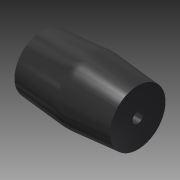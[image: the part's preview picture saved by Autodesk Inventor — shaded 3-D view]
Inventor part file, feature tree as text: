
AUTODESK INVENTOR PART (.ipt)
format: ipt  version: 2014 SP2 (Build 180246200, 246)  size: 101,376 bytes
history: native  units: mm
features: sketch x5, extrude x2, chamfer x2, fillet x1, projected_geometry x1
ambient origin geometry x8: Origin, YZ Plane, XZ Plane, XY Plane, X Axis, Y Axis, Z Axis, Center Point
bodies: Solid1 (feature_tree)
feature tree (11):
  sketch  "Sketch1"  dims[d1=18.0mm d2=0.0mm d4=18.0mm d5=0.0mm]
  sketch  "Sketch2"  dims[d6=9.0mm d7=2.0mm d8=0.872665mm d9=9.0mm d10=2.0mm d11=0.872665mm]
  extrude  "Extrusion1"  Depth=18.0mm TaperAngle=0.0deg
  sketch  "Sketch4"
  extrude  "Extrusion2"  Depth=9.0mm
  chamfer  "Chamfer1"  [1 undecoded]
  chamfer  "Chamfer2"  [1 undecoded]
  fillet  "Fillet1"  [1 undecoded]
  sketch  "Sketch3"  dims[d12=10.0mm]
  projected_geometry  "Projected Loop1"
  sketch  "Sketch5"
note: 3 required parameter values undecoded (feature->parameter linkage not recoverable at this tier; creation-order binding heuristic only, values carry confidence <= 0.55)
